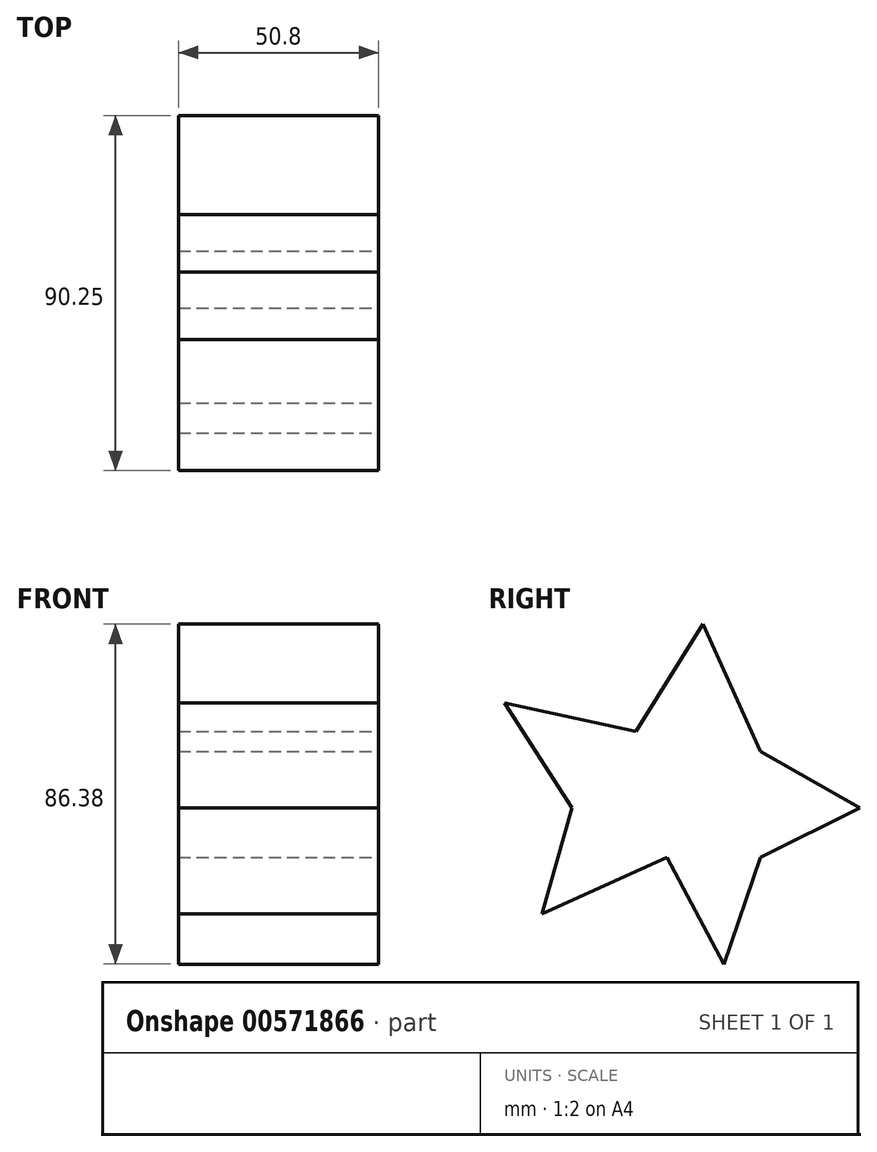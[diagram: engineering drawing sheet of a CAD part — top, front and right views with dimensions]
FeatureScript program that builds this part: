
annotation { "Feature Type Name" : "Feature", "Feature Type Description" : "" }
export const myFeature = defineFeature(function(context is Context, id is Id, definition is map)
    precondition{}
    {
        {
            var Q0;
            Q0=qCreatedBy(makeId("Right.planeOp"),FACE);
            var sketch = newSketch(context, id + "F0", { "sketchPlane" : qUnion([Q0])});
            skLineSegment(sketch, "E0", {"start": v(0, 0) * mm, "end": v(-17.18, 26.69) * mm});
            skLineSegment(sketch, "E1", {"start": v(-17.18, 26.69) * mm, "end": v(16.17, 19.43) * mm});
            skLineSegment(sketch, "E2", {"start": v(16.17, 19.43) * mm, "end": v(33.26, 46.75) * mm});
            skLineSegment(sketch, "E3", {"start": v(33.26, 46.75) * mm, "end": v(47.87, 14.36) * mm});
            skLineSegment(sketch, "E4", {"start": v(47.87, 14.36) * mm, "end": v(73.07, 0) * mm});
            skLineSegment(sketch, "E5", {"start": v(73.07, 0) * mm, "end": v(47.87, -12.58) * mm});
            skLineSegment(sketch, "E6", {"start": v(47.87, -12.58) * mm, "end": v(38.56, -39.63) * mm});
            skLineSegment(sketch, "E7", {"start": v(38.56, -39.63) * mm, "end": v(24.12, -12.58) * mm});
            skLineSegment(sketch, "E8", {"start": v(24.12, -12.58) * mm, "end": v(-7.68, -26.82) * mm});
            skLineSegment(sketch, "E9", {"start": v(-7.68, -26.82) * mm, "end": v(0, 0) * mm});
            skSolve(sketch);
        }
        {
            var Q0;
            Q0=makeQuery(id+"F0.imprint","IMPRINT",FACE,{"disambiguationData":[TD([[makeQuery(id+"F0.imprint","IMPRINT",EDGE,{"derivedFrom":sQuery(id+"F0.wireOp",EDGE,"E0")}),-1.0]])]});
            extrude(context, id + "F1", {"entities" : qUnion([Q0]), "oppositeDirection" : true, "depth" : 50.8 * mm, "offsetDistance" : 25.4 * mm});
        }
    });
